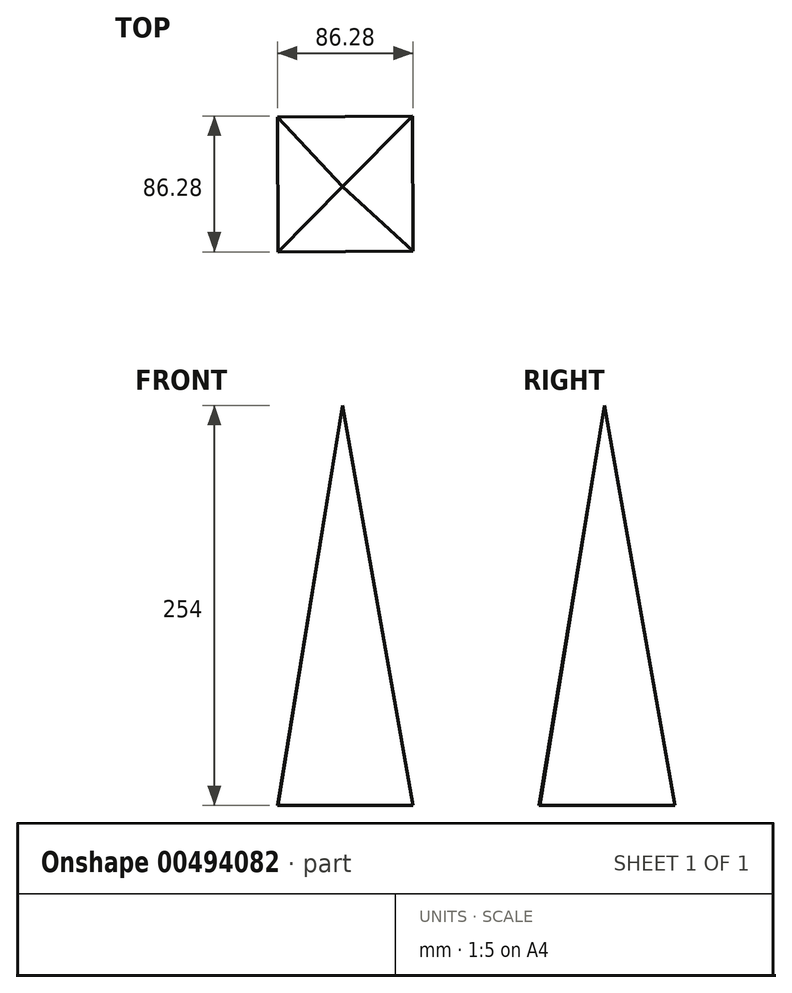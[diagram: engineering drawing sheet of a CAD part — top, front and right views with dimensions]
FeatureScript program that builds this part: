
annotation { "Feature Type Name" : "Feature", "Feature Type Description" : "" }
export const myFeature = defineFeature(function(context is Context, id is Id, definition is map)
    precondition{}
    {
        {
            var Q0;
            Q0=qCreatedBy(makeId("Top.planeOp"),FACE);
            var sketch = newSketch(context, id + "F0", { "sketchPlane" : qUnion([Q0])});
            skCircle(sketch, "E0.cCircle", {"center": v(0, 0) * mm, "radius": 60.7 * mm, "construction": true});
            skLineSegment(sketch, "E0.0", {"start": v(-43.14, 42.7) * mm, "end": v(42.7, 43.14) * mm});
            skLineSegment(sketch, "E0.1", {"start": v(42.7, 43.14) * mm, "end": v(43.14, -42.7) * mm});
            skLineSegment(sketch, "E0.2", {"start": v(43.14, -42.7) * mm, "end": v(-42.7, -43.14) * mm});
            skLineSegment(sketch, "E0.3", {"start": v(-42.7, -43.14) * mm, "end": v(-43.14, 42.7) * mm});
            skSolve(sketch);
        }
        {
            var Q0;
            Q0=qCreatedBy(makeId("Top.planeOp"),FACE);
            cPlane(context, id + "F1", {"entities" : qUnion([Q0]), "cplaneType" : CPlaneType.OFFSET, "offset" : 254 * mm, "width" : 152.4 * mm, "height" : 152.4 * mm});
        }
        {
            var Q0;
            Q0=qCreatedBy(id+"F1.planeOp",FACE);
            var sketch = newSketch(context, id + "F2", { "sketchPlane" : qUnion([Q0])});
            skPoint(sketch, "E1", {"position": v(-1.83, -1.54) * mm});
            skSolve(sketch);
        }
        {
            var Q0;
            Q0=sQuery(id+"F2.wireOp",VERTEX,"E1");
            var Q1;
            Q1=makeQuery(id+"F0.imprint","IMPRINT",FACE,{"disambiguationData":[TD([[makeQuery(id+"F0.imprint","IMPRINT",EDGE,{"derivedFrom":sQuery(id+"F0.wireOp",EDGE,"E0.0")}),-1.0]])]});
            loft(context, id + "F3", {"sheetProfilesArray" : [{ "sheetProfileEntities" : qUnion([Q0]) }, { "sheetProfileEntities" : qUnion([Q1]) }]});
        }
    });
